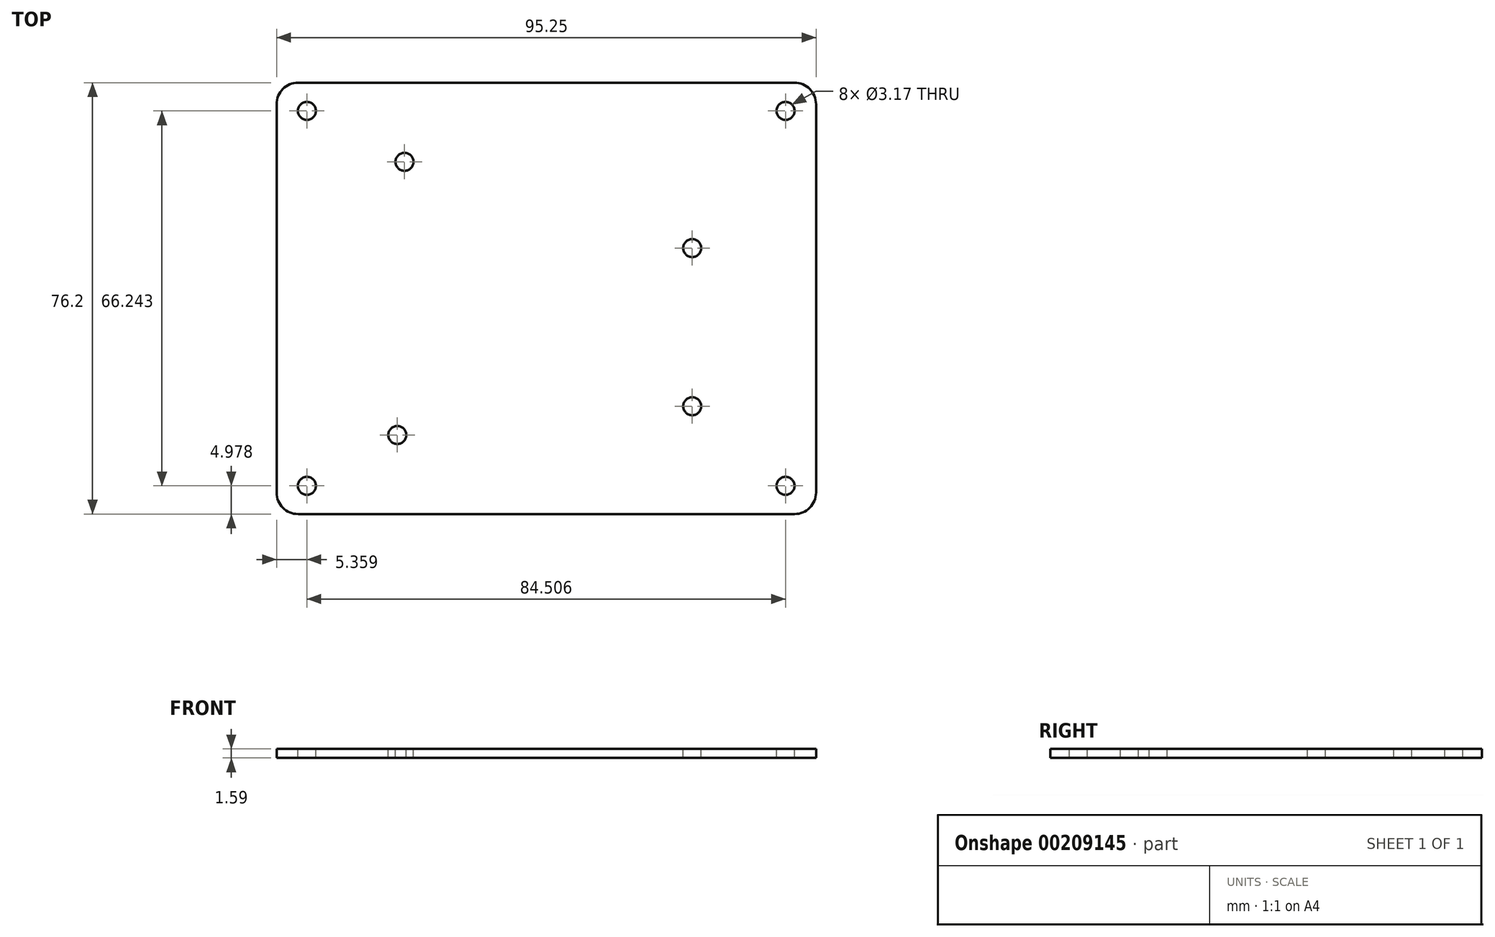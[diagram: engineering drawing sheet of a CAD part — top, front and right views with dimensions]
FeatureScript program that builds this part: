
annotation { "Feature Type Name" : "Feature", "Feature Type Description" : "" }
export const myFeature = defineFeature(function(context is Context, id is Id, definition is map)
    precondition{}
    {
        {
            var Q0;
            Q0=qCreatedBy(makeId("Top.planeOp"),FACE);
            var sketch = newSketch(context, id + "F0", { "sketchPlane" : qUnion([Q0])});
            skLineSegment(sketch, "E0.bottom", {"start": v(3.81, 0) * mm, "end": v(91.44, 0) * mm});
            skLineSegment(sketch, "E0.top", {"start": v(3.81, 76.2) * mm, "end": v(91.44, 76.2) * mm});
            skLineSegment(sketch, "E0.left", {"start": v(0, 3.81) * mm, "end": v(0, 72.4) * mm});
            skLineSegment(sketch, "E0.right", {"start": v(95.25, 3.81) * mm, "end": v(95.25, 72.4) * mm});
            skPoint(sketch, "E1.visualSharp", {"position": v(0, 76.2) * mm});
            skArc(sketch, "E1.filletArc", {"start": v(3.81, 76.2) * mm, "mid": v(1.12, 75.08) * mm, "end": v(0, 72.4) * mm});
            skPoint(sketch, "E2.visualSharp", {"position": v(95.25, 76.2) * mm});
            skArc(sketch, "E2.filletArc", {"start": v(95.25, 72.4) * mm, "mid": v(94.13, 75.08) * mm, "end": v(91.44, 76.2) * mm});
            skPoint(sketch, "E3.visualSharp", {"position": v(95.25, 0) * mm});
            skArc(sketch, "E3.filletArc", {"start": v(91.44, 0) * mm, "mid": v(94.13, 1.12) * mm, "end": v(95.25, 3.81) * mm});
            skPoint(sketch, "E4.visualSharp", {"position": v(0, 0) * mm});
            skArc(sketch, "E4.filletArc", {"start": v(0, 3.8) * mm, "mid": v(1.12, 1.12) * mm, "end": v(3.81, 0) * mm});
            skPoint(sketch, "E5", {"position": v(5.36, 71.22) * mm});
            skPoint(sketch, "E6", {"position": v(89.87, 71.22) * mm});
            skPoint(sketch, "E7", {"position": v(89.87, 4.98) * mm});
            skPoint(sketch, "E8", {"position": v(5.36, 4.98) * mm});
            skPoint(sketch, "E9", {"position": v(21.32, 13.97) * mm});
            skPoint(sketch, "E10", {"position": v(73.39, 19.05) * mm});
            skPoint(sketch, "E11", {"position": v(73.39, 47) * mm});
            skPoint(sketch, "E12", {"position": v(22.59, 62.23) * mm});
            skSolve(sketch);
        }
        {
            var Q0;
            Q0=makeQuery(id+"F0.imprint","IMPRINT",FACE,{"disambiguationData":[TD([[makeQuery(id+"F0.imprint","IMPRINT",EDGE,{"derivedFrom":sQuery(id+"F0.wireOp",EDGE,"E0.bottom")}),1.0]])]});
            extrude(context, id + "F1", {"entities" : qUnion([Q0]), "oppositeDirection" : true, "depth" : 1.59 * mm});
        }
        {
            var Q0;
            Q0=sQuery(id+"F0.wireOp",VERTEX,"E5");
            var Q1;
            Q1=sQuery(id+"F0.wireOp",VERTEX,"E12");
            var Q2;
            Q2=sQuery(id+"F0.wireOp",VERTEX,"E11");
            var Q3;
            Q3=sQuery(id+"F0.wireOp",VERTEX,"E6");
            var Q4;
            Q4=sQuery(id+"F0.wireOp",VERTEX,"E7");
            var Q5;
            Q5=sQuery(id+"F0.wireOp",VERTEX,"E10");
            var Q6;
            Q6=sQuery(id+"F0.wireOp",VERTEX,"E9");
            var Q7;
            Q7=sQuery(id+"F0.wireOp",VERTEX,"E8");
            var Q8;
            Q8=makeQuery(id+"F1.opExtrude","SWEPT_BODY",BODY,{"disambiguationData":[OSD([sQuery(id+"F0.wireOp",EDGE,"E0.bottom"),sQuery(id+"F0.wireOp",EDGE,"E0.top"),sQuery(id+"F0.wireOp",EDGE,"E0.left"),sQuery(id+"F0.wireOp",EDGE,"E0.right"),sQuery(id+"F0.wireOp",EDGE,"E1.filletArc"),sQuery(id+"F0.wireOp",EDGE,"E2.filletArc"),sQuery(id+"F0.wireOp",EDGE,"E3.filletArc"),sQuery(id+"F0.wireOp",EDGE,"E4.filletArc")])]});
            hole(context, id + "F2", {"style" : HoleStyle.SIMPLE, "endStyle" : HoleEndStyle.THROUGH, "holeDiameter" : 3.17 * mm, "locations" : qUnion([Q0, Q1, Q2, Q3, Q4, Q5, Q6, Q7]), "scope" : qUnion([Q8]), "isTappedThrough" : true});
        }
    });
